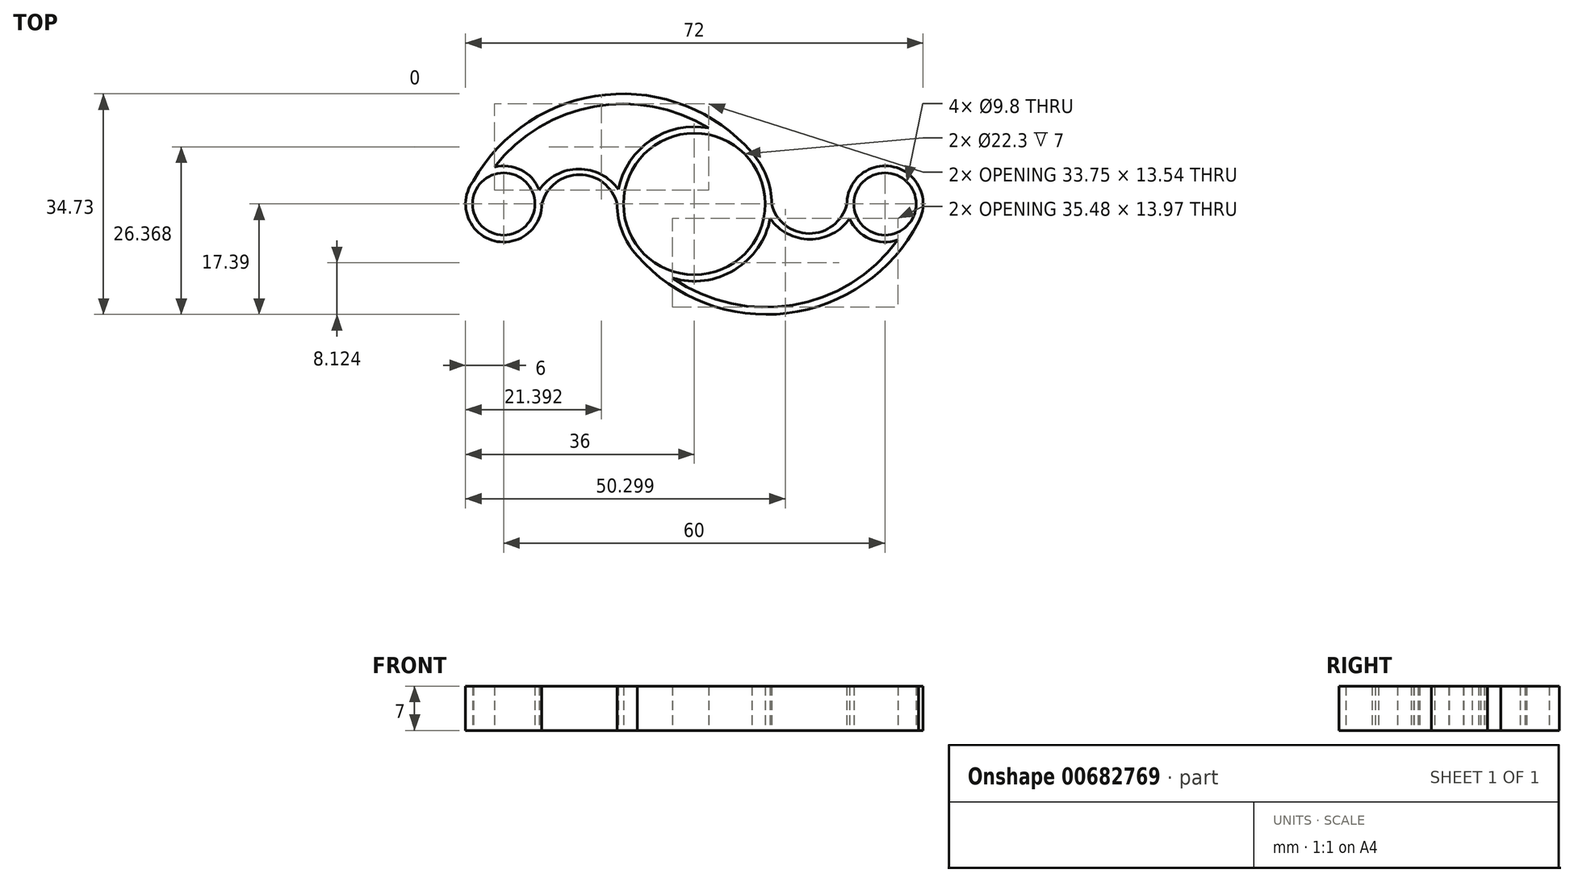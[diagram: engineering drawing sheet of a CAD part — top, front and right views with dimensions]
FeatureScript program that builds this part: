
annotation { "Feature Type Name" : "Feature", "Feature Type Description" : "" }
export const myFeature = defineFeature(function(context is Context, id is Id, definition is map)
    precondition{}
    {
        {
            var Q0;
            Q0=qCreatedBy(makeId("Top.planeOp"),FACE);
            var sketch = newSketch(context, id + "F0", { "sketchPlane" : qUnion([Q0])});
            skCircle(sketch, "E0", {"center": v(0, 0) * mm, "radius": 11.15 * mm});
            skCircle(sketch, "E1", {"center": v(0, 0) * mm, "radius": 12.15 * mm});
            skCircle(sketch, "E2", {"center": v(-30, 0) * mm, "radius": 4.9 * mm});
            skCircle(sketch, "E3.MirrorC", {"center": v(30, 0) * mm, "radius": 4.9 * mm});
            skCircle(sketch, "E4", {"center": v(-30, 0) * mm, "radius": 6 * mm});
            skCircle(sketch, "E5.MirrorC", {"center": v(30, 0) * mm, "radius": 6 * mm});
            skArc(sketch, "E6", {"start": v(9.08, 8.08) * mm, "mid": v(-14, 17.2) * mm, "end": v(-34.78, 3.62) * mm});
            skArc(sketch, "E7", {"start": v(2.27, 11.94) * mm, "mid": v(-15.78, 15.34) * mm, "end": v(-31.48, 5.81) * mm});
            skArc(sketch, "E8", {"start": v(-12.15, 0) * mm, "mid": v(-18.07, 4.61) * mm, "end": v(-24, 0) * mm});
            skArc(sketch, "E9", {"start": v(-11.93, 2.28) * mm, "mid": v(-18.2, 5.5) * mm, "end": v(-24.42, 2.2) * mm});
            skArc(sketch, "E10", {"start": v(-8.99, -8.17) * mm, "mid": v(14.65, -17.19) * mm, "end": v(35.37, -2.67) * mm});
            skArc(sketch, "E11", {"start": v(-3.44, -11.65) * mm, "mid": v(15.53, -15.9) * mm, "end": v(32.04, -5.64) * mm});
            skArc(sketch, "E12", {"start": v(12.15, 0) * mm, "mid": v(18.05, -4.65) * mm, "end": v(24, -0.08) * mm});
            skArc(sketch, "E13", {"start": v(11.93, -2.28) * mm, "mid": v(18.2, -5.55) * mm, "end": v(24.45, -2.28) * mm});
            skSolve(sketch);
        }
        {
            var Q0;
            Q0 = qSketchRegion(id + "F0", true);
            extrude(context, id + "F1", {"entities" : qUnion([Q0]), "depth" : 7 * mm, "offsetDistance" : 25 * mm});
        }
    });
